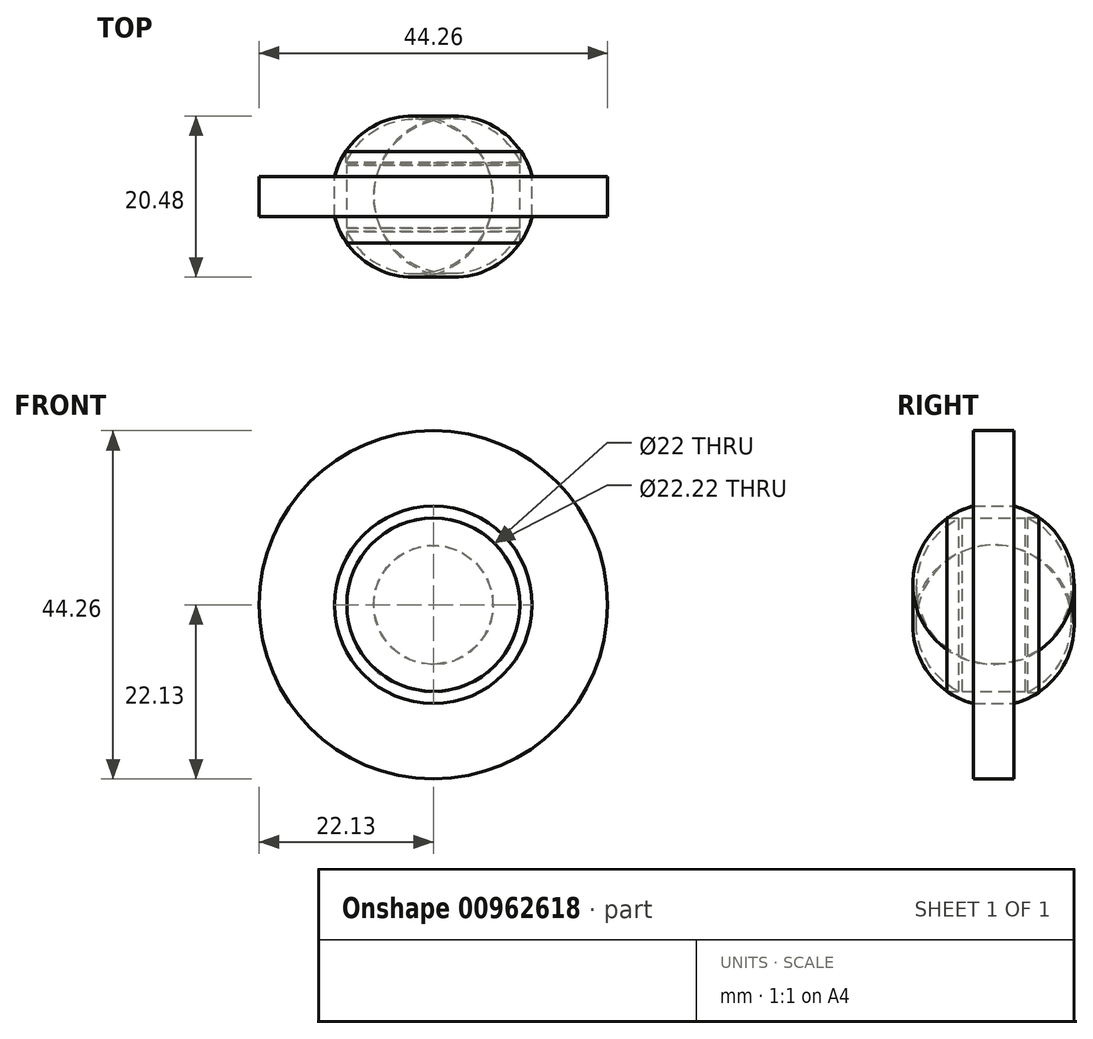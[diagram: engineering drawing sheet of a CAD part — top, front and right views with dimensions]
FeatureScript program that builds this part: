
annotation { "Feature Type Name" : "Feature", "Feature Type Description" : "" }
export const myFeature = defineFeature(function(context is Context, id is Id, definition is map)
    precondition{}
    {
        {
            var Q0;
            Q0=qCreatedBy(makeId("Front.planeOp"),FACE);
            var sketch = newSketch(context, id + "F0", { "sketchPlane" : qUnion([Q0])});
            skCircle(sketch, "E0", {"center": v(0, 0) * mm, "radius": 11 * mm});
            skSolve(sketch);
        }
        {
            var Q0;
            Q0 = qSketchRegion(id + "F0", true);
            extrude(context, id + "F1", {"entities" : qUnion([Q0]), "depth" : 8 * mm, "offsetDistance" : 25.4 * mm});
        }
        {
            var Q0;
            Q0=qCreatedBy(makeId("Right.planeOp"),FACE);
            var sketch = newSketch(context, id + "F2", { "sketchPlane" : qUnion([Q0])});
            skArc(sketch, "E1", {"start": v(1.72, 11.11) * mm, "mid": v(-4.12, 12.87) * mm, "end": v(-9.92, 11) * mm});
            skPoint(sketch, "E2.start.orphan", {"position": v(0, 11.11) * mm});
            skLineSegment(sketch, "E3", {"start": v(1.72, 11.11) * mm, "end": v(0.3, 11.11) * mm});
            skLineSegment(sketch, "E4", {"start": v(-9.92, 11) * mm, "end": v(-8.5, 11) * mm});
            skArc(sketch, "E5", {"start": v(0.3, 11.11) * mm, "mid": v(-4.11, 12.1) * mm, "end": v(-8.5, 11) * mm});
            skLineSegment(sketch, "E6.bottom", {"start": v(-1.46, 12.54) * mm, "end": v(-6.57, 12.54) * mm});
            skLineSegment(sketch, "E6.top", {"start": v(-1.46, 22.13) * mm, "end": v(-6.57, 22.13) * mm});
            skLineSegment(sketch, "E6.left", {"start": v(-1.46, 12.54) * mm, "end": v(-1.46, 22.13) * mm});
            skLineSegment(sketch, "E6.right", {"start": v(-6.57, 12.54) * mm, "end": v(-6.57, 22.13) * mm});
            skSolve(sketch);
        }
        {
            var Q0;
            {var subQ4=sQuery(id+"F2.wireOp",EDGE,"E6.top");Q0=makeQuery(id+"F2.imprint","IMPRINT",FACE,{"disambiguationData":[TD([[makeQuery(id+"F2.imprint","IMPRINT",EDGE,{"derivedFrom":subQ4}),1.0]])]});}
            var Q1;
            {var subQ1=sQuery(id+"F2.wireOp",EDGE,"E3");Q1=makeQuery(id+"F2.imprint","IMPRINT",FACE,{"disambiguationData":[TD([[makeQuery(id+"F2.imprint","IMPRINT",EDGE,{"derivedFrom":subQ1}),-1.0]])]});}
            var Q2;
            Q2=makeQuery(id+"F1.opExtrude","CAP_EDGE",EDGE,{"disambiguationData":[OSD([sQuery(id+"F0.wireOp",EDGE,"E0")])],"isStart":false});
            revolve(context, id + "F3", {"surfaceOperationType" : NewSurfaceOperationType.NEW, "entities" : qUnion([Q0, Q1]), "axis" : qUnion([Q2]), "revolveType" : RevolveType.FULL});
        }
    });
